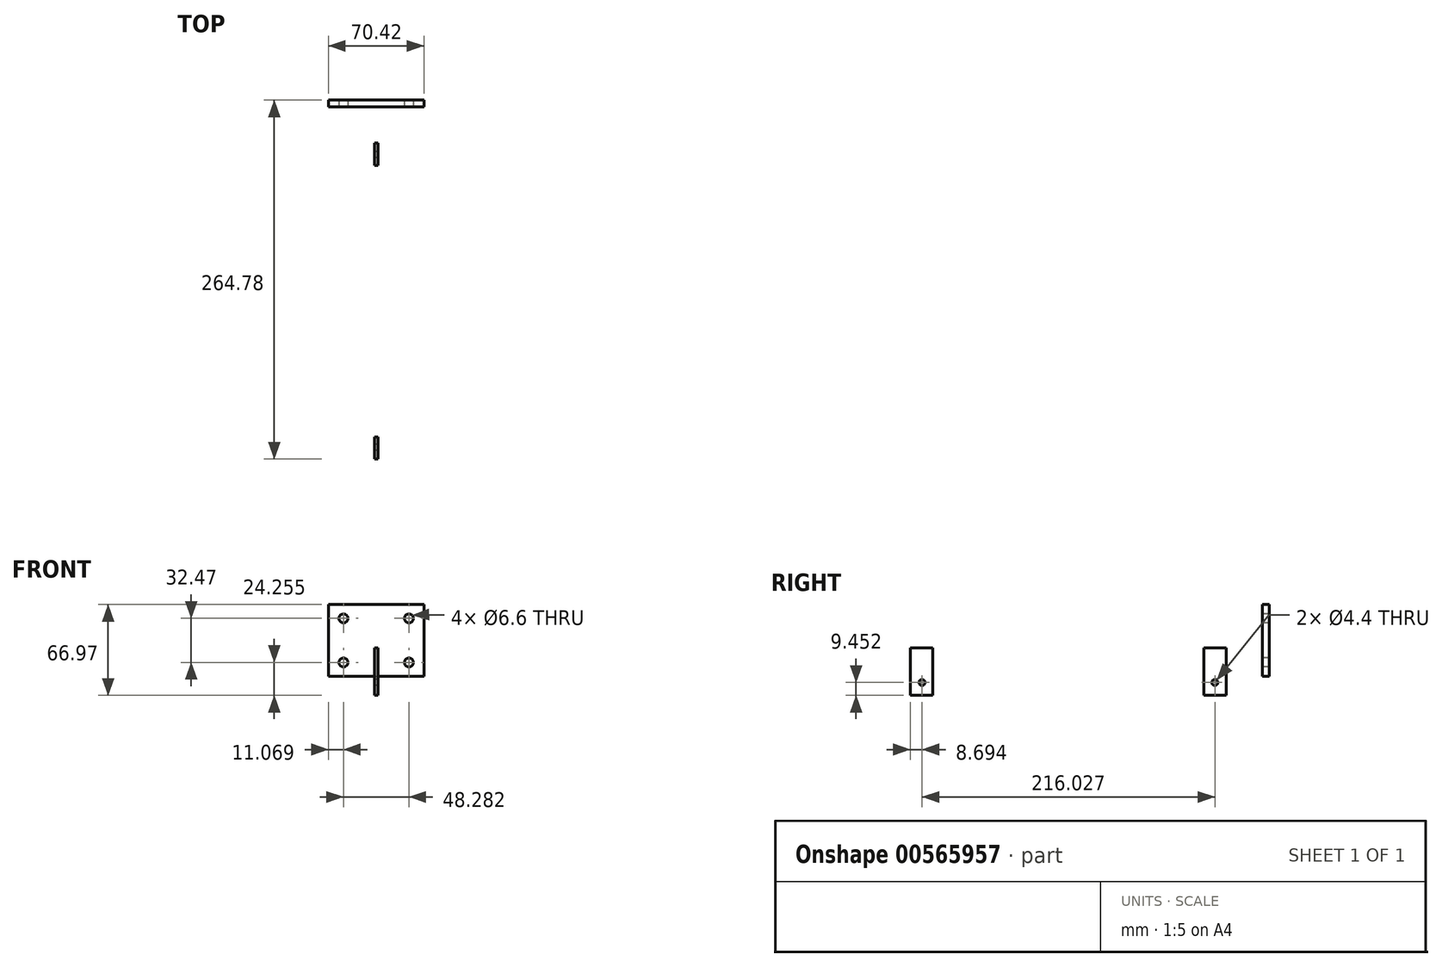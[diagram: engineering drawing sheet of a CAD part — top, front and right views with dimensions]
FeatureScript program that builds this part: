
annotation { "Feature Type Name" : "Feature", "Feature Type Description" : "" }
export const myFeature = defineFeature(function(context is Context, id is Id, definition is map)
    precondition{}
    {
        {
            var Q0;
            Q0=qCreatedBy(makeId("Front.planeOp"),FACE);
            var sketch = newSketch(context, id + "F0", { "sketchPlane" : qUnion([Q0])});
            skLineSegment(sketch, "E0.bottom", {"start": v(-35.21, 26.48) * mm, "end": v(35.21, 26.48) * mm});
            skLineSegment(sketch, "E0.top", {"start": v(-35.21, -26.48) * mm, "end": v(35.21, -26.48) * mm});
            skLineSegment(sketch, "E0.left", {"start": v(-35.21, 26.48) * mm, "end": v(-35.21, -26.48) * mm});
            skLineSegment(sketch, "E0.right", {"start": v(35.21, 26.48) * mm, "end": v(35.21, -26.48) * mm});
            skPoint(sketch, "E0.middle", {"position": v(0, 0) * mm});
            skLineSegment(sketch, "E1", {"start": v(-35.21, 26.48) * mm, "end": v(35.21, -26.48) * mm});
            skLineSegment(sketch, "E2", {"start": v(35.21, 26.48) * mm, "end": v(-35.21, -26.48) * mm});
            skLineSegment(sketch, "E3", {"start": v(-35.21, 26.48) * mm, "end": v(-25.06, 18.85) * mm});
            skSolve(sketch);
        }
        {
            var Q0;
            Q0 = qSketchRegion(id + "F0", true);
            extrude(context, id + "F1", {"entities" : qUnion([Q0]), "endBound" : BoundingType.SYMMETRIC, "depth" : 5.08 * mm, "offsetDistance" : 25.4 * mm});
        }
        {
            var Q0;
            Q0=makeQuery(id+"F1.opExtrude","CAP_FACE",FACE,{"disambiguationData":[OSD([sQuery(id+"F0.wireOp",EDGE,"E0.bottom"),sQuery(id+"F0.wireOp",EDGE,"E0.top"),sQuery(id+"F0.wireOp",EDGE,"E0.left"),sQuery(id+"F0.wireOp",EDGE,"E0.right")])],"isStart":false});
            var sketch = newSketch(context, id + "F2", { "sketchPlane" : qUnion([Q0])});
            skPoint(sketch, "E4", {"position": v(-24.14, 16.23) * mm});
            skPoint(sketch, "E5.MirrorP", {"position": v(24.14, 16.23) * mm});
            skPoint(sketch, "E6.MirrorP", {"position": v(24.14, -16.23) * mm});
            skPoint(sketch, "E7.MirrorP", {"position": v(-24.14, -16.23) * mm});
            skSolve(sketch);
        }
        {
            var Q0;
            Q0=sQuery(id+"F2.wireOp",VERTEX,"E4");
            var Q1;
            Q1=sQuery(id+"F2.wireOp",VERTEX,"E5.MirrorP");
            var Q2;
            Q2=sQuery(id+"F2.wireOp",VERTEX,"E6.MirrorP");
            var Q3;
            Q3=sQuery(id+"F2.wireOp",VERTEX,"E7.MirrorP");
            var Q4;
            Q4=makeQuery(id+"F1.opExtrude","SWEPT_BODY",BODY,{"disambiguationData":[OSD([sQuery(id+"F0.wireOp",EDGE,"E0.bottom"),sQuery(id+"F0.wireOp",EDGE,"E0.top"),sQuery(id+"F0.wireOp",EDGE,"E0.left"),sQuery(id+"F0.wireOp",EDGE,"E0.right")])]});
            hole(context, id + "F3", {"style" : HoleStyle.SIMPLE, "endStyle" : HoleEndStyle.THROUGH, "standardTappedOrClearance" : lookupTablePath({ "standard" : "ISO", "fit" : "Normal", "size" : "M6", "type" : "Clearance" }), "standardBlindInLast" : lookupTablePath({ "fit" : "Standard", "standard" : "ISO", "size" : "M6", "type" : "Clearance" }), "holeDiameter" : 6.6 * mm, "isTappedThrough" : true, "tappedDepth" : 12.7 * mm, "tapClearance" : 3, "startFromSketch" : true, "locations" : qUnion([Q0, Q1, Q2, Q3]), "scope" : qUnion([Q4])});
        }
        {
            var Q0;
            Q0=makeQuery(id+"F1.opExtrude","CAP_FACE",FACE,{"disambiguationData":[OSD([sQuery(id+"F0.wireOp",EDGE,"E0.bottom"),sQuery(id+"F0.wireOp",EDGE,"E0.top"),sQuery(id+"F0.wireOp",EDGE,"E0.left"),sQuery(id+"F0.wireOp",EDGE,"E0.right")])],"isStart":false});
            var sketch = newSketch(context, id + "F4", { "sketchPlane" : qUnion([Q0])});
            skCircle(sketch, "E8", {"center": v(0, 0) * mm, "radius": 3.86 * mm});
            skCircle(sketch, "E9", {"center": v(0, 0) * mm, "radius": 5.18 * mm});
            skSolve(sketch);
        }
        {
            var Q0;
            Q0=sQuery(id+"F4.wireOp",EDGE,"E8");
            extrude(context, id + "F5", {"bodyType" : ToolBodyType.SURFACE, "surfaceEntities" : qUnion([Q0]), "depth" : 254 * mm, "offsetDistance" : 25.4 * mm});
        }
        {
            var Q0;
            Q0=sQuery(id+"F4.wireOp",EDGE,"E9");
            extrude(context, id + "F6", {"bodyType" : ToolBodyType.SURFACE, "surfaceEntities" : qUnion([Q0]), "depth" : 274.32 * mm, "offsetDistance" : 25.4 * mm});
        }
        {
            var Q0;
            Q0=qCreatedBy(makeId("Right.planeOp"),FACE);
            var sketch = newSketch(context, id + "F7", { "sketchPlane" : qUnion([Q0])});
            skLineSegment(sketch, "E10.bottom", {"start": v(-29.14, -5.41) * mm, "end": v(-45.59, -5.41) * mm});
            skLineSegment(sketch, "E10.top", {"start": v(-29.14, -40.35) * mm, "end": v(-45.59, -40.35) * mm});
            skLineSegment(sketch, "E10.left", {"start": v(-29.14, -5.41) * mm, "end": v(-29.14, -40.35) * mm});
            skLineSegment(sketch, "E10.right", {"start": v(-45.59, -5.41) * mm, "end": v(-45.59, -40.35) * mm});
            skLineSegment(sketch, "E11.bottom", {"start": v(-248.63, -5.33) * mm, "end": v(-265.08, -5.33) * mm});
            skLineSegment(sketch, "E11.top", {"start": v(-248.63, -40.27) * mm, "end": v(-265.08, -40.27) * mm});
            skLineSegment(sketch, "E11.left", {"start": v(-248.63, -5.33) * mm, "end": v(-248.63, -40.27) * mm});
            skLineSegment(sketch, "E11.right", {"start": v(-265.08, -5.33) * mm, "end": v(-265.08, -40.27) * mm});
            skSolve(sketch);
        }
        {
            var Q0;
            Q0=makeQuery(id+"F7.imprint","IMPRINT",FACE,{"disambiguationData":[TD([[makeQuery(id+"F7.imprint","IMPRINT",EDGE,{"derivedFrom":sQuery(id+"F7.wireOp",EDGE,"E10.bottom")}),1.0]])]});
            extrude(context, id + "F8", {"entities" : qUnion([Q0]), "endBound" : BoundingType.SYMMETRIC, "depth" : 2.54 * mm, "offsetDistance" : 25.4 * mm});
        }
        {
            var Q0;
            Q0=makeQuery(id+"F8.opExtrude","CAP_FACE",FACE,{"disambiguationData":[OSD([sQuery(id+"F7.wireOp",EDGE,"E10.bottom"),sQuery(id+"F7.wireOp",EDGE,"E10.top"),sQuery(id+"F7.wireOp",EDGE,"E10.left"),sQuery(id+"F7.wireOp",EDGE,"E10.right")])],"isStart":true});
            var sketch = newSketch(context, id + "F9", { "sketchPlane" : qUnion([Q0])});
            skPoint(sketch, "E12", {"position": v(37.52, -31.04) * mm});
            skSolve(sketch);
        }
        {
            var Q0;
            Q0=sQuery(id+"F9.wireOp",VERTEX,"E12");
            var Q1;
            Q1=makeQuery(id+"F8.opExtrude","SWEPT_BODY",BODY,{"disambiguationData":[OSD([sQuery(id+"F7.wireOp",EDGE,"E10.bottom"),sQuery(id+"F7.wireOp",EDGE,"E10.top"),sQuery(id+"F7.wireOp",EDGE,"E10.left"),sQuery(id+"F7.wireOp",EDGE,"E10.right")])]});
            hole(context, id + "F10", {"style" : HoleStyle.SIMPLE, "endStyle" : HoleEndStyle.THROUGH, "standardTappedOrClearance" : lookupTablePath({ "standard" : "ISO", "fit" : "Normal", "size" : "M4", "type" : "Clearance" }), "standardBlindInLast" : lookupTablePath({ "fit" : "Standard", "standard" : "ISO", "size" : "M4", "type" : "Clearance" }), "holeDiameter" : 4.4 * mm, "isTappedThrough" : true, "tappedDepth" : 12.7 * mm, "tapClearance" : 3, "startFromSketch" : true, "locations" : qUnion([Q0]), "scope" : qUnion([Q1])});
        }
        {
            var Q0;
            Q0=qCreatedBy(makeId("Right.planeOp"),FACE);
            var sketch = newSketch(context, id + "F11", { "sketchPlane" : qUnion([Q0])});
            skLineSegment(sketch, "E13.bottom", {"start": v(-245.8, -5.55) * mm, "end": v(-262.24, -5.55) * mm});
            skLineSegment(sketch, "E13.top", {"start": v(-245.8, -40.49) * mm, "end": v(-262.24, -40.49) * mm});
            skLineSegment(sketch, "E13.left", {"start": v(-245.8, -5.55) * mm, "end": v(-245.8, -40.49) * mm});
            skLineSegment(sketch, "E13.right", {"start": v(-262.24, -5.55) * mm, "end": v(-262.24, -40.49) * mm});
            skPoint(sketch, "E14", {"position": v(-254.17, -31.04) * mm});
            skSolve(sketch);
        }
        {
            var Q0;
            Q0=makeQuery(id+"F11.imprint","IMPRINT",FACE,{"disambiguationData":[TD([[makeQuery(id+"F11.imprint","IMPRINT",EDGE,{"derivedFrom":sQuery(id+"F11.wireOp",EDGE,"E13.bottom")}),1.0]])]});
            extrude(context, id + "F12", {"entities" : qUnion([Q0]), "endBound" : BoundingType.SYMMETRIC, "depth" : 2.54 * mm, "offsetDistance" : 25.4 * mm});
        }
        {
            var Q0;
            Q0=makeQuery(id+"F12.opExtrude","CAP_FACE",FACE,{"disambiguationData":[OSD([sQuery(id+"F11.wireOp",EDGE,"E13.bottom"),sQuery(id+"F11.wireOp",EDGE,"E13.top"),sQuery(id+"F11.wireOp",EDGE,"E13.left"),sQuery(id+"F11.wireOp",EDGE,"E13.right")])],"isStart":true});
            var sketch = newSketch(context, id + "F13", { "sketchPlane" : qUnion([Q0])});
            skPoint(sketch, "E15", {"position": v(253.55, -31.04) * mm});
            skSolve(sketch);
        }
        {
            var Q0;
            Q0=sQuery(id+"F13.wireOp",VERTEX,"E15");
            var Q1;
            Q1=makeQuery(id+"F12.opExtrude","SWEPT_BODY",BODY,{"disambiguationData":[OSD([sQuery(id+"F11.wireOp",EDGE,"E13.bottom"),sQuery(id+"F11.wireOp",EDGE,"E13.top"),sQuery(id+"F11.wireOp",EDGE,"E13.left"),sQuery(id+"F11.wireOp",EDGE,"E13.right")])]});
            hole(context, id + "F14", {"style" : HoleStyle.SIMPLE, "endStyle" : HoleEndStyle.THROUGH, "standardTappedOrClearance" : lookupTablePath({ "standard" : "ISO", "fit" : "Normal", "size" : "M4", "type" : "Clearance" }), "standardBlindInLast" : lookupTablePath({ "fit" : "Standard", "standard" : "ISO", "size" : "M4", "type" : "Clearance" }), "holeDiameter" : 4.4 * mm, "isTappedThrough" : true, "tappedDepth" : 12.7 * mm, "tapClearance" : 3, "startFromSketch" : true, "locations" : qUnion([Q0]), "scope" : qUnion([Q1])});
        }
    });
